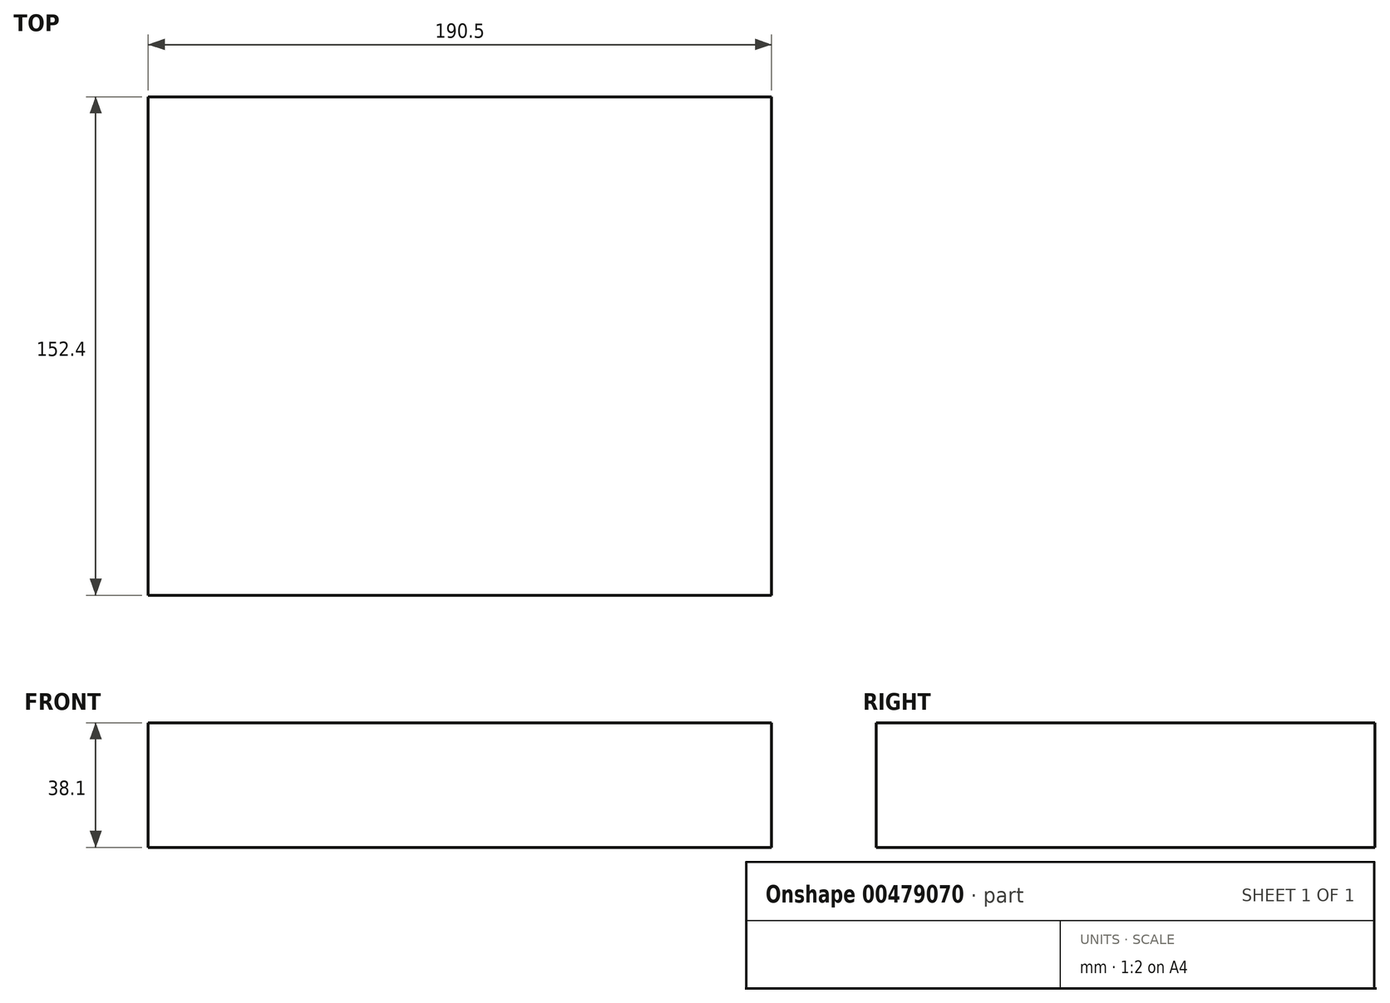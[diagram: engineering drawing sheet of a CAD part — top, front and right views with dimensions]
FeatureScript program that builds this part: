
annotation { "Feature Type Name" : "Feature", "Feature Type Description" : "" }
export const myFeature = defineFeature(function(context is Context, id is Id, definition is map)
    precondition{}
    {
        {
            var Q0;
            Q0=qCreatedBy(makeId("Top.planeOp"),FACE);
            var sketch = newSketch(context, id + "F0", { "sketchPlane" : qUnion([Q0])});
            skLineSegment(sketch, "E0.bottom", {"start": v(95.25, 76.2) * mm, "end": v(-95.25, 76.2) * mm});
            skLineSegment(sketch, "E0.top", {"start": v(95.25, -76.2) * mm, "end": v(-95.25, -76.2) * mm});
            skLineSegment(sketch, "E0.left", {"start": v(95.25, 76.2) * mm, "end": v(95.25, -76.2) * mm});
            skLineSegment(sketch, "E0.right", {"start": v(-95.25, 76.2) * mm, "end": v(-95.25, -76.2) * mm});
            skPoint(sketch, "E0.middle", {"position": v(0, 0) * mm});
            skSolve(sketch);
        }
        {
            var Q0;
            Q0=makeQuery(id+"F0.imprint","IMPRINT",FACE,{"disambiguationData":[TD([[makeQuery(id+"F0.imprint","IMPRINT",EDGE,{"derivedFrom":sQuery(id+"F0.wireOp",EDGE,"E0.bottom")}),1.0]])]});
            extrude(context, id + "F1", {"entities" : qUnion([Q0]), "depth" : 38.1 * mm});
        }
    });
